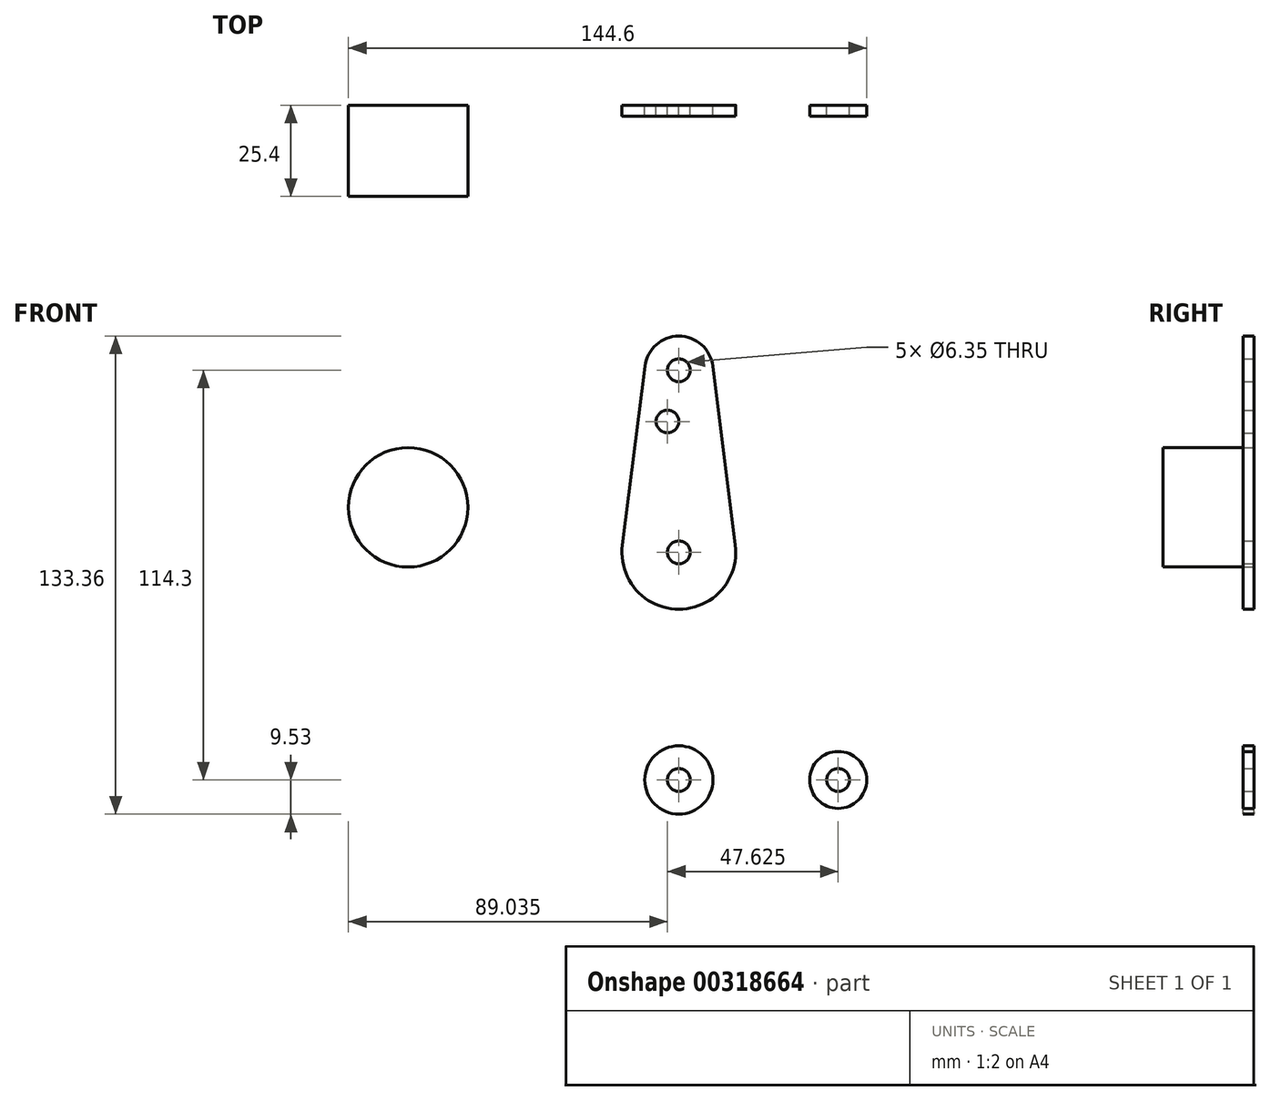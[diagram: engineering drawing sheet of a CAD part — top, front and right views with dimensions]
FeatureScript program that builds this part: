
annotation { "Feature Type Name" : "Feature", "Feature Type Description" : "" }
export const myFeature = defineFeature(function(context is Context, id is Id, definition is map)
    precondition{}
    {
        {
            var Q0;
            Q0=qCreatedBy(makeId("Front.planeOp"),FACE);
            var sketch = newSketch(context, id + "F0", { "sketchPlane" : qUnion([Q0])});
            skLineSegment(sketch, "E0", {"start": v(0, 0) * mm, "end": v(44.45, 0) * mm, "construction": true});
            skLineSegment(sketch, "E1", {"start": v(0, 0) * mm, "end": v(0, 114.3) * mm, "construction": true});
            skCircle(sketch, "E2", {"center": v(0, 114.3) * mm, "radius": 9.53 * mm});
            skCircle(sketch, "E3", {"center": v(0, 63.5) * mm, "radius": 15.88 * mm});
            skCircle(sketch, "E4", {"center": v(0, 0) * mm, "radius": 9.53 * mm});
            skCircle(sketch, "E5", {"center": v(44.45, 0) * mm, "radius": 7.94 * mm});
            skLineSegment(sketch, "E6", {"start": v(0, -9.53) * mm, "end": v(44.73, -7.93) * mm});
            skLineSegment(sketch, "E7", {"start": v(15.75, 65.48) * mm, "end": v(9.45, 115.5) * mm});
            skLineSegment(sketch, "E8", {"start": v(-9.45, 115.5) * mm, "end": v(-15.75, 65.48) * mm});
            skLineSegment(sketch, "E9", {"start": v(-9.53, 0) * mm, "end": v(-15.75, 61.47) * mm});
            skCircle(sketch, "E10", {"center": v(0, 114.3) * mm, "radius": 3.18 * mm});
            skCircle(sketch, "E11", {"center": v(0, 63.5) * mm, "radius": 3.18 * mm});
            skCircle(sketch, "E12", {"center": v(0, 0) * mm, "radius": 3.18 * mm});
            skCircle(sketch, "E13", {"center": v(44.45, 0) * mm, "radius": 3.18 * mm});
            skCircle(sketch, "E14", {"center": v(-3.18, 100.03) * mm, "radius": 3.18 * mm});
            skLineSegment(sketch, "E15", {"start": v(11.3, 17.6) * mm, "end": v(15.75, 61.47) * mm});
            skLineSegment(sketch, "E16", {"start": v(44.73, 7.93) * mm, "end": v(18.93, 8.85) * mm});
            skArc(sketch, "E17.filletArc", {"start": v(11.3, 17.6) * mm, "mid": v(13.22, 11.57) * mm, "end": v(18.93, 8.85) * mm});
            skSolve(sketch);
        }
        {
            var Q0;
            Q0 = qSketchRegion(id + "F0", true);
            extrude(context, id + "F1", {"entities" : qUnion([Q0]), "depth" : 3.05 * mm});
        }
        {
            var Q0;
            Q0=qCreatedBy(makeId("Front.planeOp"),FACE);
            var sketch = newSketch(context, id + "F2", { "sketchPlane" : qUnion([Q0])});
            skCircle(sketch, "E18", {"center": v(-75.55, 76.06) * mm, "radius": 16.66 * mm});
            skSolve(sketch);
        }
        {
            var Q0;
            Q0 = qSketchRegion(id + "F2", true);
            extrude(context, id + "F3", {"entities" : qUnion([Q0]), "depth" : 25.4 * mm});
        }
    });
